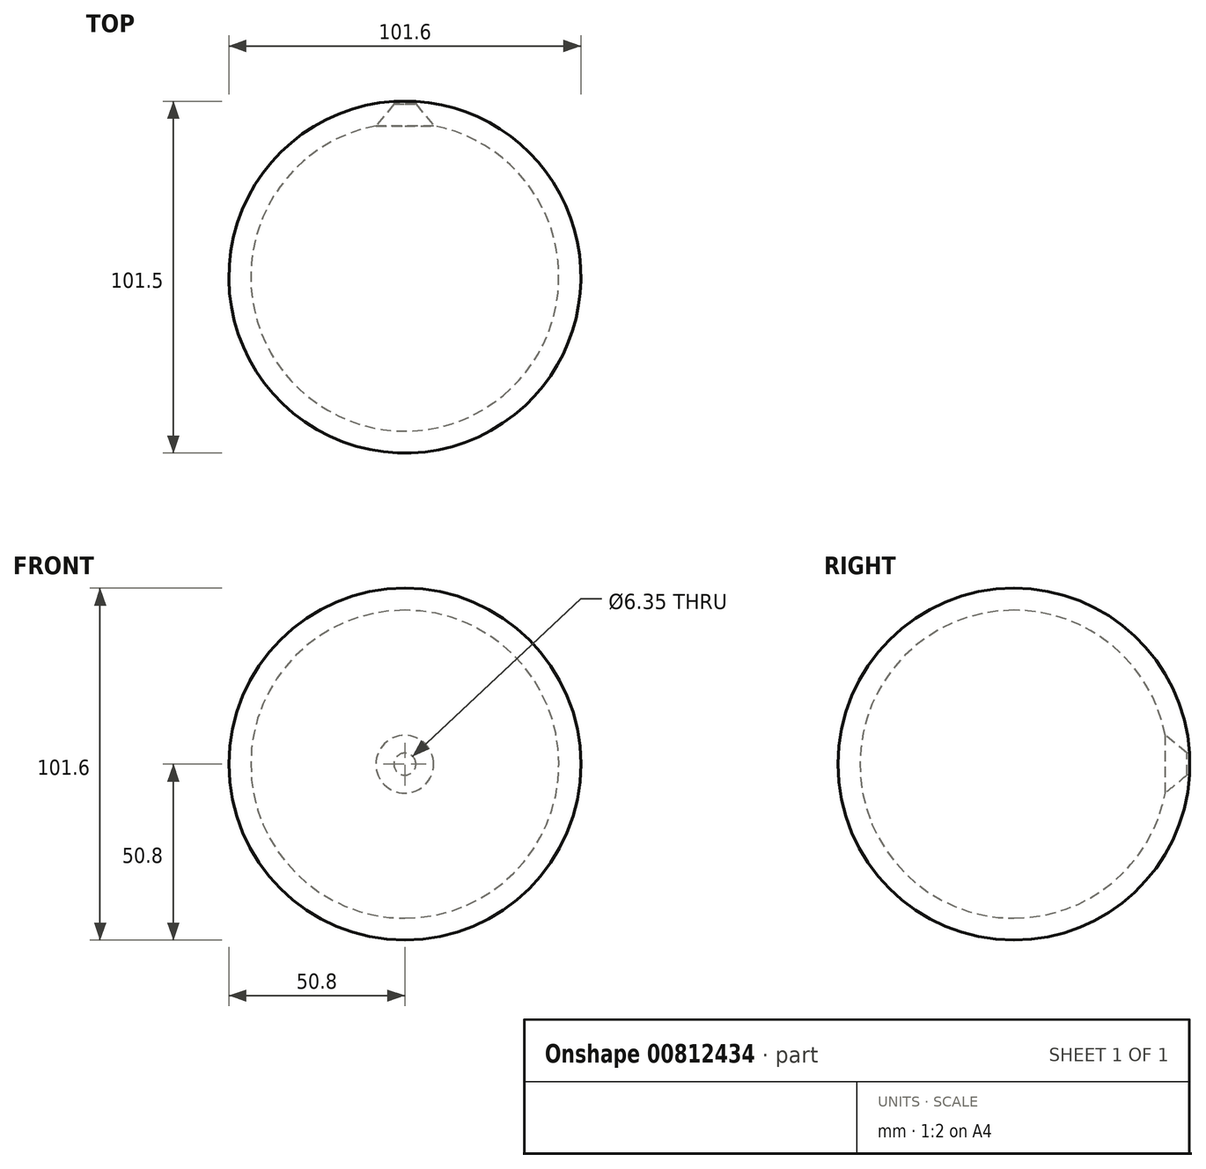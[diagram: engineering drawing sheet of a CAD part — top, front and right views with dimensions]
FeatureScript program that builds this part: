
annotation { "Feature Type Name" : "Feature", "Feature Type Description" : "" }
export const myFeature = defineFeature(function(context is Context, id is Id, definition is map)
    precondition{}
    {
        {
            var Q0;
            Q0=qCreatedBy(makeId("Front.planeOp"),FACE);
            var sketch = newSketch(context, id + "F0", { "sketchPlane" : qUnion([Q0])});
            skArc(sketch, "E0", {"start": v(0, 50.8) * mm, "mid": v(50.8, 0) * mm, "end": v(0, -50.8) * mm});
            skArc(sketch, "E1", {"start": v(0, 44.45) * mm, "mid": v(44.45, 0) * mm, "end": v(0, -44.45) * mm});
            skLineSegment(sketch, "E2", {"start": v(0, 50.8) * mm, "end": v(0, 44.45) * mm});
            skLineSegment(sketch, "E3", {"start": v(0, -44.45) * mm, "end": v(0, -50.8) * mm});
            skLineSegment(sketch, "E4", {"start": v(0, 50.8) * mm, "end": v(0, -50.8) * mm, "construction": true});
            skSolve(sketch);
        }
        {
            var Q0;
            Q0 = qSketchRegion(id + "F0", true);
            var Q1;
            Q1=sQuery(id+"F0.wireOp",EDGE,"E4");
            revolve(context, id + "F1", {"surfaceOperationType" : NewSurfaceOperationType.NEW, "entities" : qUnion([Q0]), "axis" : qUnion([Q1]), "revolveType" : RevolveType.FULL});
        }
        {
            var Q0;
            Q0=qCreatedBy(makeId("Front.planeOp"),FACE);
            var sketch = newSketch(context, id + "F2", { "sketchPlane" : qUnion([Q0])});
            skCircle(sketch, "E5", {"center": v(0, 0) * mm, "radius": 3.18 * mm});
            skSolve(sketch);
        }
        {
            var Q0;
            Q0 = qSketchRegion(id + "F2", true);
            extrude(context, id + "F3", {"entities" : qUnion([Q0]), "operationType" : NewBodyOperationType.REMOVE, "oppositeDirection" : true, "depth" : 101.6 * mm, "offsetDistance" : 25.4 * mm});
        }
        {
            var Q0;
            Q0=makeQuery(id+"F3.boolean.opBoolean","INTERSECT",EDGE,{"derivedFrom":[makeQuery(id+"F1.opRevolve","SWEPT_FACE",FACE,{"disambiguationData":[OSD([sQuery(id+"F0.wireOp",EDGE,"E1")])]}),makeQuery(id+"F3.opExtrude","SWEPT_FACE",FACE,{"disambiguationData":[OSD([sQuery(id+"F2.wireOp",EDGE,"E5")])]})]});
            chamfer(context, id + "F4", {"entities" : qUnion([Q0]), "width" : 6.35 * mm, "tangentPropagation" : true});
        }
    });
